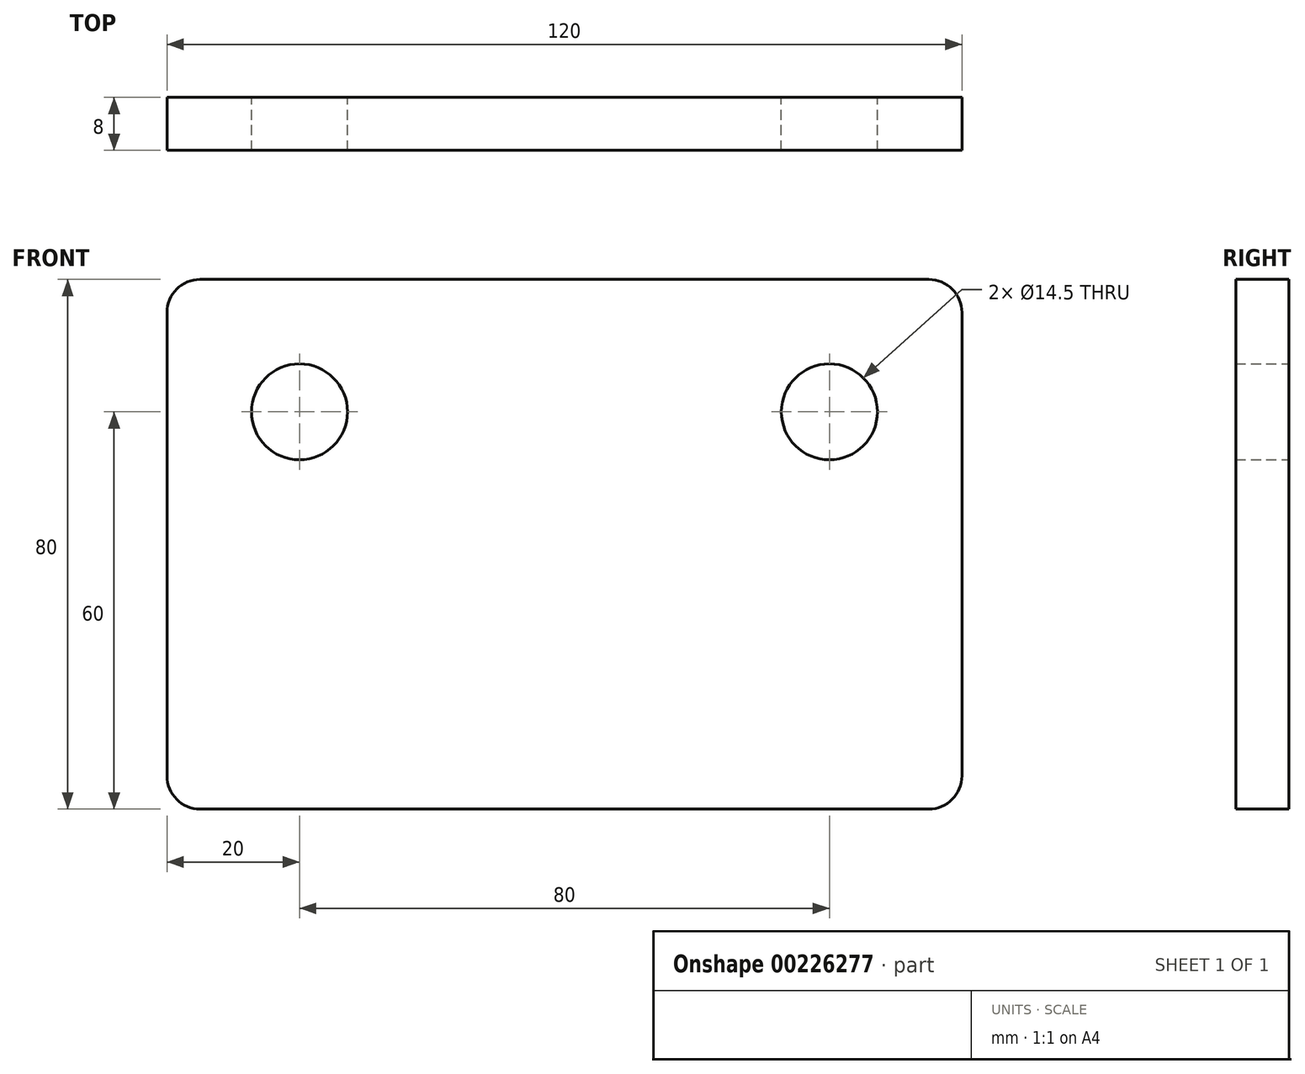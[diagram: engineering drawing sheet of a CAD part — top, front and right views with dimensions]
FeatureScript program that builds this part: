
annotation { "Feature Type Name" : "Feature", "Feature Type Description" : "" }
export const myFeature = defineFeature(function(context is Context, id is Id, definition is map)
    precondition{}
    {
        {
            var Q0;
            Q0=qCreatedBy(makeId("Front.planeOp"),FACE);
            var sketch = newSketch(context, id + "F0", { "sketchPlane" : qUnion([Q0])});
            skLineSegment(sketch, "E0.bottom", {"start": v(55, 40) * mm, "end": v(-55, 40) * mm});
            skLineSegment(sketch, "E0.top", {"start": v(55, -40) * mm, "end": v(-55, -40) * mm});
            skLineSegment(sketch, "E0.left", {"start": v(60, 35) * mm, "end": v(60, -35) * mm});
            skLineSegment(sketch, "E0.right", {"start": v(-60, 35) * mm, "end": v(-60, -35) * mm});
            skPoint(sketch, "E0.middle", {"position": v(0, 0) * mm});
            skPoint(sketch, "E1.visualSharp", {"position": v(-60, 40) * mm});
            skArc(sketch, "E1.filletArc", {"start": v(-55, 40) * mm, "mid": v(-58.54, 38.54) * mm, "end": v(-60, 35) * mm});
            skArc(sketch, "E2.filletArc", {"start": v(-60, -35) * mm, "mid": v(-58.54, -38.54) * mm, "end": v(-55, -40) * mm});
            skPoint(sketch, "E3.visualSharp", {"position": v(60, -40) * mm});
            skArc(sketch, "E3.filletArc", {"start": v(55, -40) * mm, "mid": v(58.54, -38.54) * mm, "end": v(60, -35) * mm});
            skPoint(sketch, "E4.visualSharp", {"position": v(60, 40) * mm});
            skArc(sketch, "E4.filletArc", {"start": v(60, 35) * mm, "mid": v(58.54, 38.54) * mm, "end": v(55, 40) * mm});
            skCircle(sketch, "E5", {"center": v(-40, 20) * mm, "radius": 7.25 * mm});
            skCircle(sketch, "E6.1.0.0", {"center": v(40, 20) * mm, "radius": 7.25 * mm});
            skLineSegment(sketch, "E6.direction1", {"start": v(-40, 20) * mm, "end": v(40, 20) * mm, "construction": true});
            skSolve(sketch);
        }
        {
            var Q0;
            Q0=makeQuery(id+"F0.imprint","IMPRINT",FACE,{"disambiguationData":[TD([[makeQuery(id+"F0.imprint","IMPRINT",EDGE,{"derivedFrom":sQuery(id+"F0.wireOp",EDGE,"E0.bottom")}),1.0]])]});
            extrude(context, id + "F1", {"entities" : qUnion([Q0]), "depth" : 8 * mm});
        }
    });
